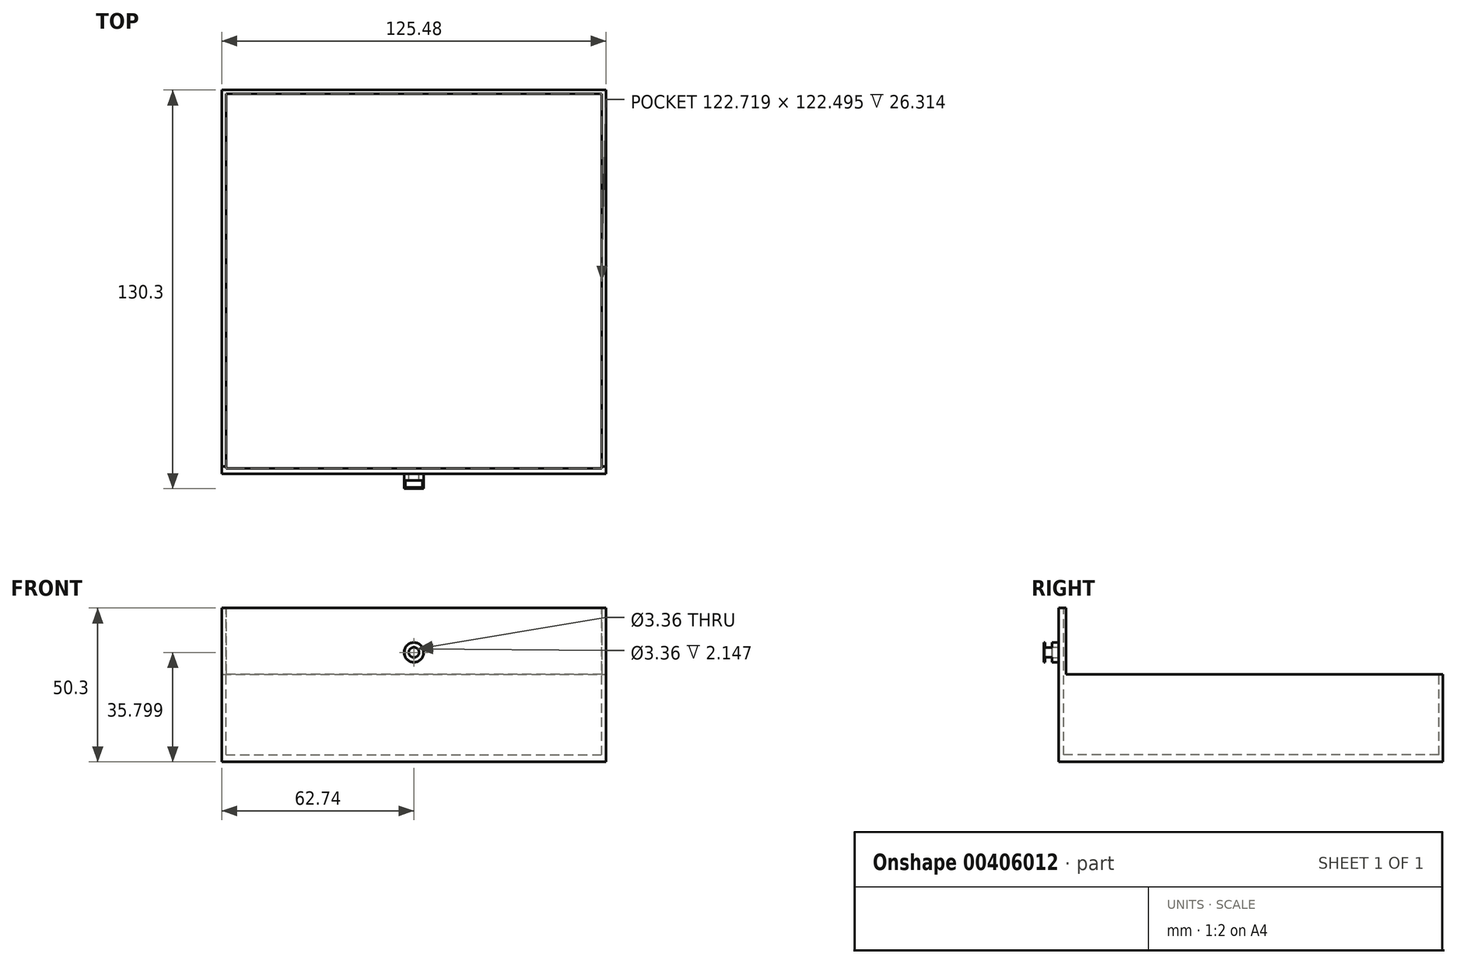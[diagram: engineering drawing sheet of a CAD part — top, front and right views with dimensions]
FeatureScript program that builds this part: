
annotation { "Feature Type Name" : "Feature", "Feature Type Description" : "" }
export const myFeature = defineFeature(function(context is Context, id is Id, definition is map)
    precondition{}
    {
        {
            var Q0;
            Q0=qCreatedBy(makeId("Front.planeOp"),FACE);
            var sketch = newSketch(context, id + "F0", { "sketchPlane" : qUnion([Q0])});
            skLineSegment(sketch, "E0.bottom", {"start": v(62.74, -25.15) * mm, "end": v(-62.74, -25.15) * mm});
            skLineSegment(sketch, "E0.top", {"start": v(62.74, 25.15) * mm, "end": v(-62.74, 25.15) * mm});
            skLineSegment(sketch, "E0.left", {"start": v(62.74, -25.15) * mm, "end": v(62.74, 25.15) * mm});
            skLineSegment(sketch, "E0.right", {"start": v(-62.74, -25.15) * mm, "end": v(-62.74, 25.15) * mm});
            skPoint(sketch, "E0.middle", {"position": v(0, 0) * mm});
            skSolve(sketch);
        }
        {
            var Q0;
            Q0 = qSketchRegion(id + "F0", true);
            extrude(context, id + "F1", {"entities" : qUnion([Q0]), "depth" : 125.48 * mm});
        }
        {
            var Q0;
            Q0=makeQuery(id+"F1.opExtrude","SWEPT_FACE",FACE,{"disambiguationData":[OSD([sQuery(id+"F0.wireOp",EDGE,"E0.top")])]});
            var sketch = newSketch(context, id + "F2", { "sketchPlane" : qUnion([Q0])});
            skLineSegment(sketch, "E1.bottom", {"start": v(-61.36, -1.23) * mm, "end": v(61.36, -1.23) * mm});
            skLineSegment(sketch, "E1.top", {"start": v(-61.36, -123.72) * mm, "end": v(61.36, -123.72) * mm});
            skLineSegment(sketch, "E1.left", {"start": v(-61.36, -1.23) * mm, "end": v(-61.36, -123.72) * mm});
            skLineSegment(sketch, "E1.right", {"start": v(61.36, -1.23) * mm, "end": v(61.36, -123.72) * mm});
            skSolve(sketch);
        }
        {
            var Q0;
            Q0 = qSketchRegion(id + "F2", true);
            var Q1;
            Q1 = qSketchRegion(id + "F4", true);
            extrude(context, id + "F3", {"entities" : qUnion([Q0, Q1]), "operationType" : NewBodyOperationType.REMOVE, "oppositeDirection" : true, "depth" : 48 * mm});
        }
        {
            var Q0;
            Q0=makeQuery(id+"F1.opExtrude","CAP_FACE",FACE,{"disambiguationData":[OSD([sQuery(id+"F0.wireOp",EDGE,"E0.bottom"),sQuery(id+"F0.wireOp",EDGE,"E0.top"),sQuery(id+"F0.wireOp",EDGE,"E0.left"),sQuery(id+"F0.wireOp",EDGE,"E0.right")])],"isStart":false});
            var sketch = newSketch(context, id + "F4", { "sketchPlane" : qUnion([Q0])});
            skSolve(sketch);
        }
        {
            var Q0;
            Q0=makeQuery(id+"F4.imprint","IMPRINT",FACE,{"disambiguationData":[TD([[makeQuery(id+"F4.imprint","IMPRINT",EDGE,{"derivedFrom":makeQuery(id+"F1.opExtrude","CAP_EDGE",EDGE,{"disambiguationData":[OSD([sQuery(id+"F0.wireOp",EDGE,"E0.bottom")])],"isStart":false})}),-1.0]])]});
            var sketch = newSketch(context, id + "F5", { "sketchPlane" : qUnion([Q0])});
            skCircle(sketch, "E2", {"center": v(0, 10.65) * mm, "radius": 3.22 * mm});
            skCircle(sketch, "E3", {"center": v(0, 10.65) * mm, "radius": 1.68 * mm});
            skSolve(sketch);
        }
        {
            var Q0;
            Q0 = qSketchRegion(id + "F5", true);
            extrude(context, id + "F6", {"entities" : qUnion([Q0]), "operationType" : NewBodyOperationType.ADD, "depth" : 4.83 * mm});
        }
        {
            var Q0;
            Q0=makeQuery(id+"F1.opExtrude","SWEPT_FACE",FACE,{"disambiguationData":[OSD([sQuery(id+"F0.wireOp",EDGE,"E0.left")])]});
            var sketch = newSketch(context, id + "F7", { "sketchPlane" : qUnion([Q0])});
            skLineSegment(sketch, "E4.bottom", {"start": v(0, 3.45) * mm, "end": v(-80.56, 3.45) * mm});
            skLineSegment(sketch, "E4.top", {"start": v(0, 25.15) * mm, "end": v(-80.56, 25.15) * mm});
            skLineSegment(sketch, "E4.left", {"start": v(0, 3.45) * mm, "end": v(0, 25.15) * mm});
            skLineSegment(sketch, "E4.right", {"start": v(-80.56, 3.45) * mm, "end": v(-80.56, 25.15) * mm});
            skSolve(sketch);
        }
        {
            var Q0;
            Q0 = qSketchRegion(id + "F7", true);
            extrude(context, id + "F8", {"entities" : qUnion([Q0]), "operationType" : NewBodyOperationType.REMOVE, "endBound" : BoundingType.THROUGH_ALL, "oppositeDirection" : true, "depth" : 25.4 * mm});
        }
        {
            var Q0;
            Q0=makeQuery(id+"F1.opExtrude","SWEPT_FACE",FACE,{"disambiguationData":[OSD([sQuery(id+"F0.wireOp",EDGE,"E0.left")])]});
            var sketch = newSketch(context, id + "F9", { "sketchPlane" : qUnion([Q0])});
            skLineSegment(sketch, "E5.bottom", {"start": v(-80.56, 3.45) * mm, "end": v(-123.04, 3.45) * mm});
            skLineSegment(sketch, "E5.top", {"start": v(-80.56, 28.5) * mm, "end": v(-123.04, 28.5) * mm});
            skLineSegment(sketch, "E5.left", {"start": v(-80.56, 3.45) * mm, "end": v(-80.56, 28.5) * mm});
            skLineSegment(sketch, "E5.right", {"start": v(-123.04, 3.45) * mm, "end": v(-123.04, 28.5) * mm});
            skSolve(sketch);
        }
        {
            var Q0;
            Q0 = qSketchRegion(id + "F9", true);
            extrude(context, id + "F10", {"entities" : qUnion([Q0]), "operationType" : NewBodyOperationType.REMOVE, "endBound" : BoundingType.THROUGH_ALL, "oppositeDirection" : true, "depth" : 25.4 * mm});
        }
        {
            var Q0;
            Q0=makeQuery(id+"F3.boolean.opBoolean","COPY",FACE,{"derivedFrom":makeQuery(id+"F3.opExtrude","CAP_FACE",FACE,{"disambiguationData":[OSD([sQuery(id+"F2.wireOp",EDGE,"E1.bottom"),sQuery(id+"F2.wireOp",EDGE,"E1.top"),sQuery(id+"F2.wireOp",EDGE,"E1.left"),sQuery(id+"F2.wireOp",EDGE,"E1.right")])],"isStart":false})});
            var sketch = newSketch(context, id + "F11", { "sketchPlane" : qUnion([Q0])});
            skLineSegment(sketch, "E6.bottom", {"start": v(2.82, -129.87) * mm, "end": v(-2.83, -129.87) * mm});
            skLineSegment(sketch, "E6.top", {"start": v(2.82, -127.62) * mm, "end": v(-2.83, -127.62) * mm});
            skLineSegment(sketch, "E6.left", {"start": v(2.82, -129.87) * mm, "end": v(2.82, -127.62) * mm});
            skLineSegment(sketch, "E6.right", {"start": v(-2.83, -129.87) * mm, "end": v(-2.83, -127.62) * mm});
            skSolve(sketch);
        }
        {
            var Q0;
            Q0 = qSketchRegion(id + "F11", true);
            extrude(context, id + "F12", {"entities" : qUnion([Q0]), "operationType" : NewBodyOperationType.REMOVE, "endBound" : BoundingType.THROUGH_ALL, "depth" : 25.4 * mm});
        }
    });
